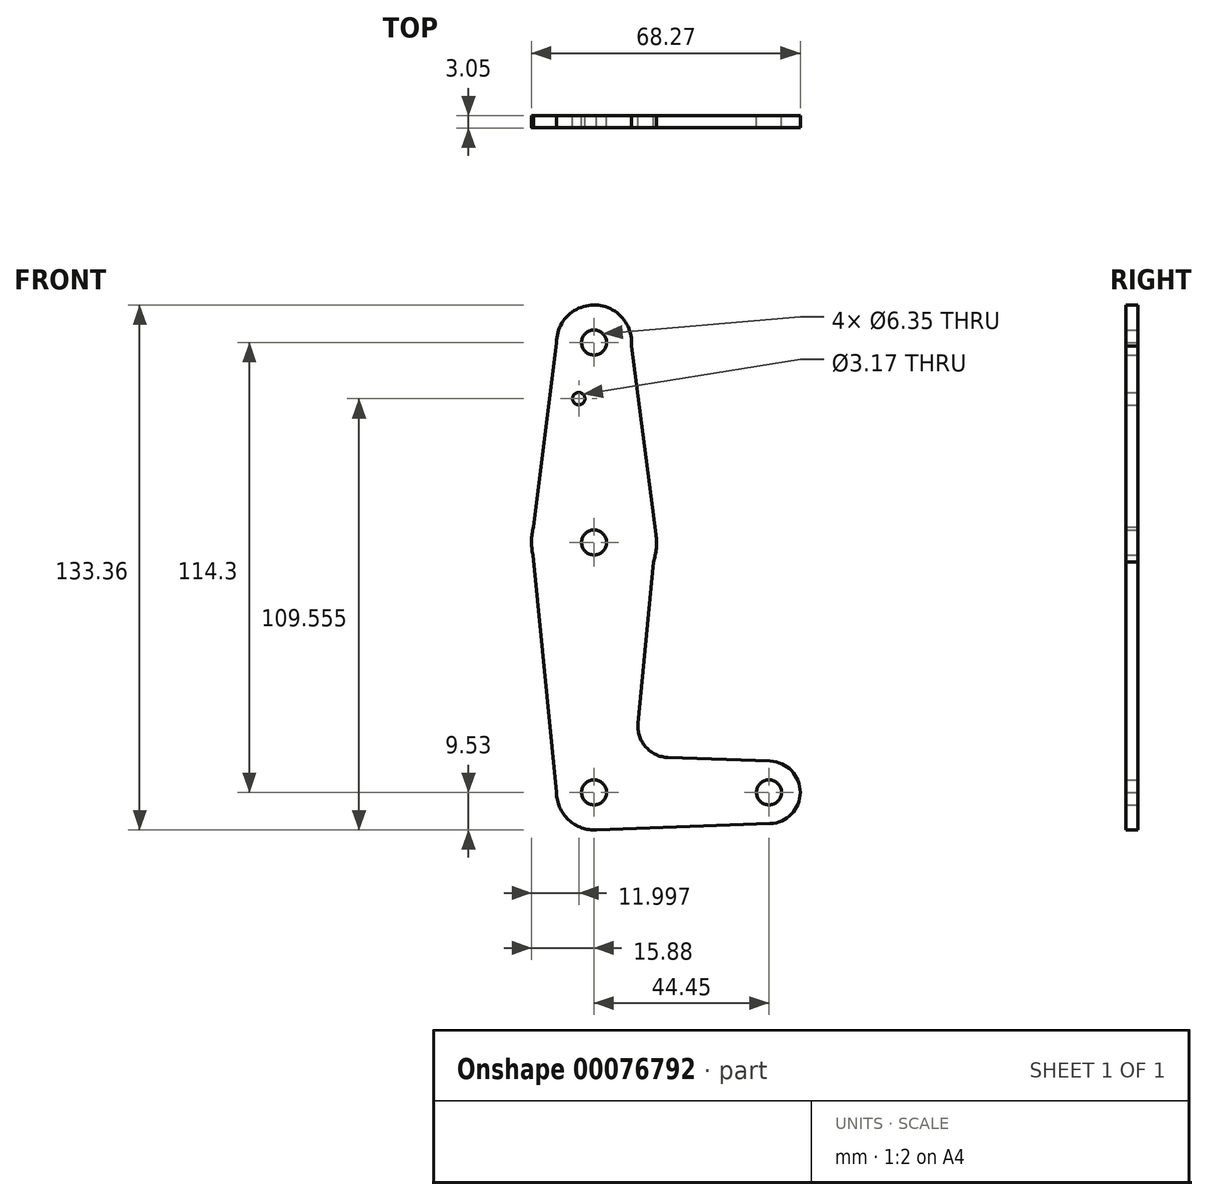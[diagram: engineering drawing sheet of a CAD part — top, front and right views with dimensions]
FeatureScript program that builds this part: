
annotation { "Feature Type Name" : "Feature", "Feature Type Description" : "" }
export const myFeature = defineFeature(function(context is Context, id is Id, definition is map)
    precondition{}
    {
        {
            var Q0;
            Q0=qCreatedBy(makeId("Front.planeOp"),FACE);
            var sketch = newSketch(context, id + "F0", { "sketchPlane" : qUnion([Q0])});
            skLineSegment(sketch, "E0", {"start": v(0, 0) * mm, "end": v(0, 114.3) * mm, "construction": true});
            skCircle(sketch, "E1", {"center": v(0, 114.3) * mm, "radius": 9.53 * mm});
            skCircle(sketch, "E2", {"center": v(0, 0) * mm, "radius": 9.53 * mm});
            skLineSegment(sketch, "E3", {"start": v(0, 0) * mm, "end": v(44.45, 0) * mm, "construction": true});
            skCircle(sketch, "E4", {"center": v(44.45, 0) * mm, "radius": 7.94 * mm});
            skCircle(sketch, "E5", {"center": v(0, 63.5) * mm, "radius": 15.88 * mm});
            skLineSegment(sketch, "E6", {"start": v(9.48, 113.42) * mm, "end": v(15.74, 65.56) * mm});
            skLineSegment(sketch, "E7", {"start": v(15.74, 65.56) * mm, "end": v(11.18, 17.55) * mm});
            skLineSegment(sketch, "E8", {"start": v(18.81, 8.86) * mm, "end": v(44.73, 7.93) * mm});
            skLineSegment(sketch, "E9", {"start": v(0, -9.53) * mm, "end": v(44.73, -7.93) * mm});
            skCircle(sketch, "E10", {"center": v(0, 114.3) * mm, "radius": 3.18 * mm});
            skCircle(sketch, "E11", {"center": v(-3.88, 100.03) * mm, "radius": 1.59 * mm});
            skCircle(sketch, "E12", {"center": v(0, 63.5) * mm, "radius": 3.18 * mm});
            skCircle(sketch, "E13", {"center": v(0, 0) * mm, "radius": 3.18 * mm});
            skCircle(sketch, "E14", {"center": v(44.45, 0) * mm, "radius": 3.18 * mm});
            skArc(sketch, "E15.filletArc", {"start": v(11.18, 17.55) * mm, "mid": v(13.12, 11.56) * mm, "end": v(18.81, 8.86) * mm});
            skLineSegment(sketch, "E16", {"start": v(-9.52, 114.3) * mm, "end": v(-15.88, 63.5) * mm});
            skLineSegment(sketch, "E17", {"start": v(-15.88, 63.5) * mm, "end": v(-9.53, 0) * mm});
            skSolve(sketch);
        }
        {
            var Q0;
            Q0 = qSketchRegion(id + "F0", true);
            extrude(context, id + "F1", {"entities" : qUnion([Q0]), "depth" : 3.05 * mm});
        }
    });
